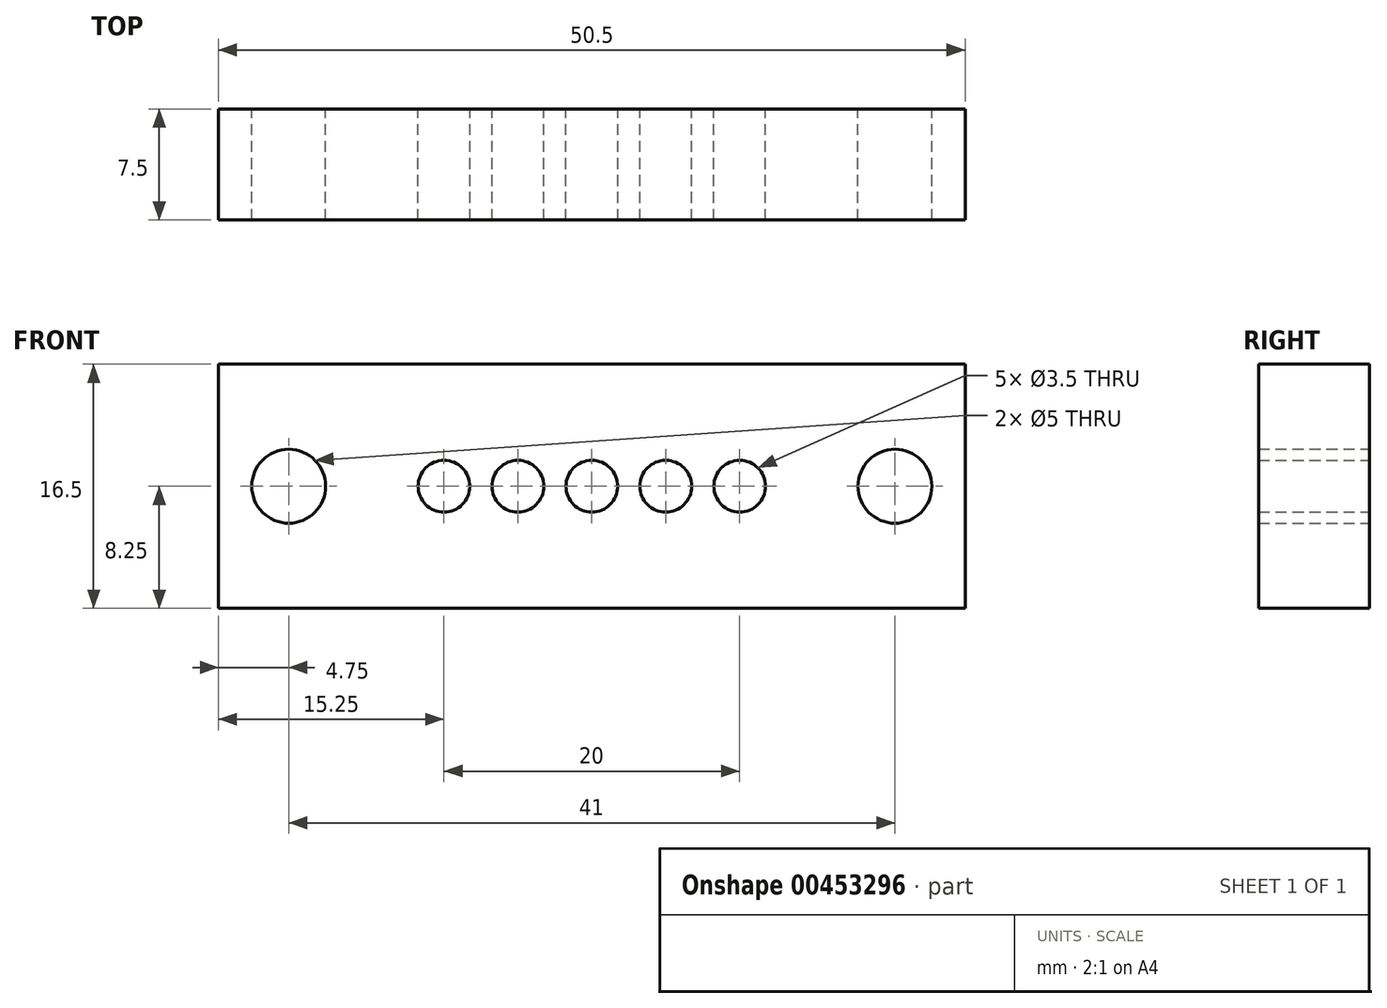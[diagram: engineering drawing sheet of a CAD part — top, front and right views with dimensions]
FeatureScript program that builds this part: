
annotation { "Feature Type Name" : "Feature", "Feature Type Description" : "" }
export const myFeature = defineFeature(function(context is Context, id is Id, definition is map)
    precondition{}
    {
        {
            var Q0;
            Q0=qCreatedBy(makeId("Front.planeOp"),FACE);
            var sketch = newSketch(context, id + "F0", { "sketchPlane" : qUnion([Q0])});
            skLineSegment(sketch, "E0.bottom", {"start": v(-23.15, 8.25) * mm, "end": v(27.35, 8.25) * mm});
            skLineSegment(sketch, "E0.top", {"start": v(-23.15, -8.25) * mm, "end": v(27.35, -8.25) * mm});
            skLineSegment(sketch, "E0.left", {"start": v(-23.15, 8.25) * mm, "end": v(-23.15, -8.25) * mm});
            skLineSegment(sketch, "E0.right", {"start": v(27.35, 8.25) * mm, "end": v(27.35, -8.25) * mm});
            skCircle(sketch, "E1", {"center": v(-7.9, 0) * mm, "radius": 1.75 * mm});
            skCircle(sketch, "E2", {"center": v(-2.9, 0) * mm, "radius": 1.75 * mm});
            skCircle(sketch, "E3", {"center": v(2.1, 0) * mm, "radius": 1.75 * mm});
            skCircle(sketch, "E4", {"center": v(7.1, 0) * mm, "radius": 1.75 * mm});
            skCircle(sketch, "E5", {"center": v(12.1, 0) * mm, "radius": 1.75 * mm});
            skCircle(sketch, "E6", {"center": v(22.6, 0) * mm, "radius": 2.5 * mm});
            skCircle(sketch, "E7", {"center": v(-18.4, 0) * mm, "radius": 2.5 * mm});
            skPoint(sketch, "E8.endSnap0", {"position": v(2.1, -8.25) * mm});
            skSolve(sketch);
        }
        {
            var Q0;
            Q0=makeQuery(id+"F0.imprint","IMPRINT",FACE,{"disambiguationData":[TD([[makeQuery(id+"F0.imprint","IMPRINT",EDGE,{"derivedFrom":sQuery(id+"F0.wireOp",EDGE,"E0.bottom")}),-1.0]])]});
            extrude(context, id + "F1", {"entities" : qUnion([Q0]), "depth" : 7.5 * mm});
        }
    });
